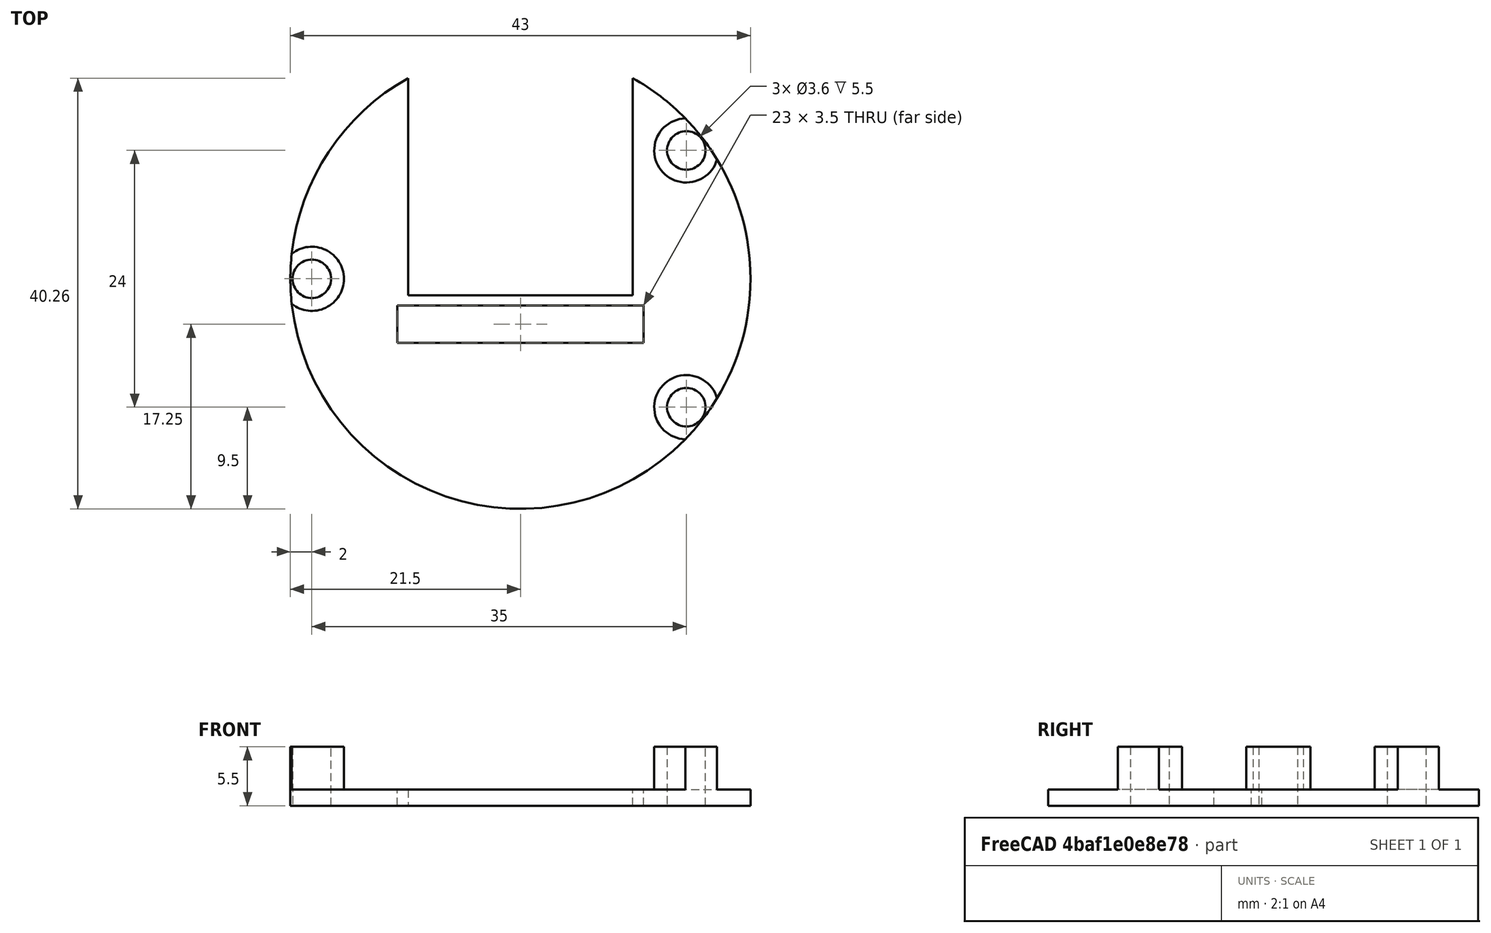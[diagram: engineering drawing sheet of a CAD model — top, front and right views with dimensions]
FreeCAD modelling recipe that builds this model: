
FCSTD DOCUMENT  (FreeCAD 0.21R33771 (Git))
Label: inner-plate3
License: All rights reserved
LicenseURL: http://en.wikipedia.org/wiki/All_rights_reserved
objects: Part::Cylinder×8, Part::Cut×7, Part::Box×3, Part::MultiFuse×3
note: 21 computed .brp shape members not serialized (recipe doc carries the construction recipe); baked Part::Feature solids carry a one-line shape summary decoded from their .brp

FEATURE [Part::Cylinder] Cylinder  label="円柱"
  Angle = 360
  AttacherType = Attacher::AttachEngine3D
  FirstAngle = 0
  Height = 1.5
  Radius = 21.5
  SecondAngle = 0
FEATURE [Part::Box] Box  label="立方体"
  AttacherType = Attacher::AttachEngine3D
  Height = 5
  Length = 21
  Placement = pos=(-10.5,-1.53,-2) rot=(0,0,1;0rad)
  Width = 25
FEATURE [Part::Cut] Cut
  Base = -> Cylinder
  Tool = -> Box
FEATURE [Part::Box] Box001  label="立方体001"
  AttacherType = Attacher::AttachEngine3D
  Height = 2
  Length = 23
  Placement = pos=(-11.5,-6,0) rot=(0,0,1;0rad)
  Width = 3.5
FEATURE [Part::Cut] Cut001
  Base = -> Cut
  Tool = -> Box001
FEATURE [Part::Cylinder] Cylinder001  label="円柱001"
  Angle = 360
  AttacherType = Attacher::AttachEngine3D
  FirstAngle = 0
  Height = 4
  Placement = pos=(-19.5,0,1.5) rot=(0,0,1;0rad)
  Radius = 3
  SecondAngle = 0
FEATURE [Part::Cylinder] Cylinder002  label="円柱002"
  Angle = 360
  AttacherType = Attacher::AttachEngine3D
  FirstAngle = 0
  Height = 10
  Placement = pos=(-19.5,0,-2) rot=(0,0,1;0rad)
  Radius = 1.8
  SecondAngle = 0
FEATURE [Part::MultiFuse] Fusion
  Shapes = -> [Cut001,Cylinder001]
FEATURE [Part::Cut] Cut002
  Base = -> Fusion
  Tool = -> Cylinder002
FEATURE [Part::Cylinder] Cylinder003  label="円柱003"
  Angle = 360
  AttacherType = Attacher::AttachEngine3D
  FirstAngle = 0
  Height = 4
  Placement = pos=(15.5,-12,1.5) rot=(0,0,1;0rad)
  Radius = 3
  SecondAngle = 0
FEATURE [Part::MultiFuse] Fusion001
  Shapes = -> [Cut002,Cylinder003]
FEATURE [Part::Cylinder] Cylinder004  label="円柱004"
  Angle = 360
  AttacherType = Attacher::AttachEngine3D
  FirstAngle = 0
  Height = 10
  Placement = pos=(15.5,-12,-2) rot=(0,0,1;0rad)
  Radius = 1.8
  SecondAngle = 0
FEATURE [Part::Cut] Cut003
  Base = -> Fusion001
  Tool = -> Cylinder004
FEATURE [Part::Cylinder] Cylinder005  label="円柱005"
  Angle = 360
  AttacherType = Attacher::AttachEngine3D
  FirstAngle = 0
  Height = 4
  Placement = pos=(15.5,12,1.5) rot=(0,0,1;0rad)
  Radius = 3
  SecondAngle = 0
FEATURE [Part::MultiFuse] Fusion002
  Shapes = -> [Cut003,Cylinder005]
FEATURE [Part::Cylinder] Cylinder006  label="円柱006"
  Angle = 360
  AttacherType = Attacher::AttachEngine3D
  FirstAngle = 0
  Height = 10
  Placement = pos=(15.5,12,-2) rot=(0,0,1;0rad)
  Radius = 1.8
  SecondAngle = 0
FEATURE [Part::Cut] Cut004
  Base = -> Fusion002
  Tool = -> Cylinder006
FEATURE [Part::Box] Box002  label="立方体002"
  AttacherType = Attacher::AttachEngine3D
  Height = 10
  Length = 50
  Placement = pos=(-25,-25,0) rot=(0,0,1;0rad)
  Width = 50
FEATURE [Part::Cylinder] Cylinder007  label="円柱007"
  Angle = 360
  AttacherType = Attacher::AttachEngine3D
  FirstAngle = 0
  Height = 10
  Radius = 21.5
  SecondAngle = 0
FEATURE [Part::Cut] Cut005
  Base = -> Box002
  Tool = -> Cylinder007
FEATURE [Part::Cut] Cut006
  Base = -> Cut004
  Tool = -> Cut005
